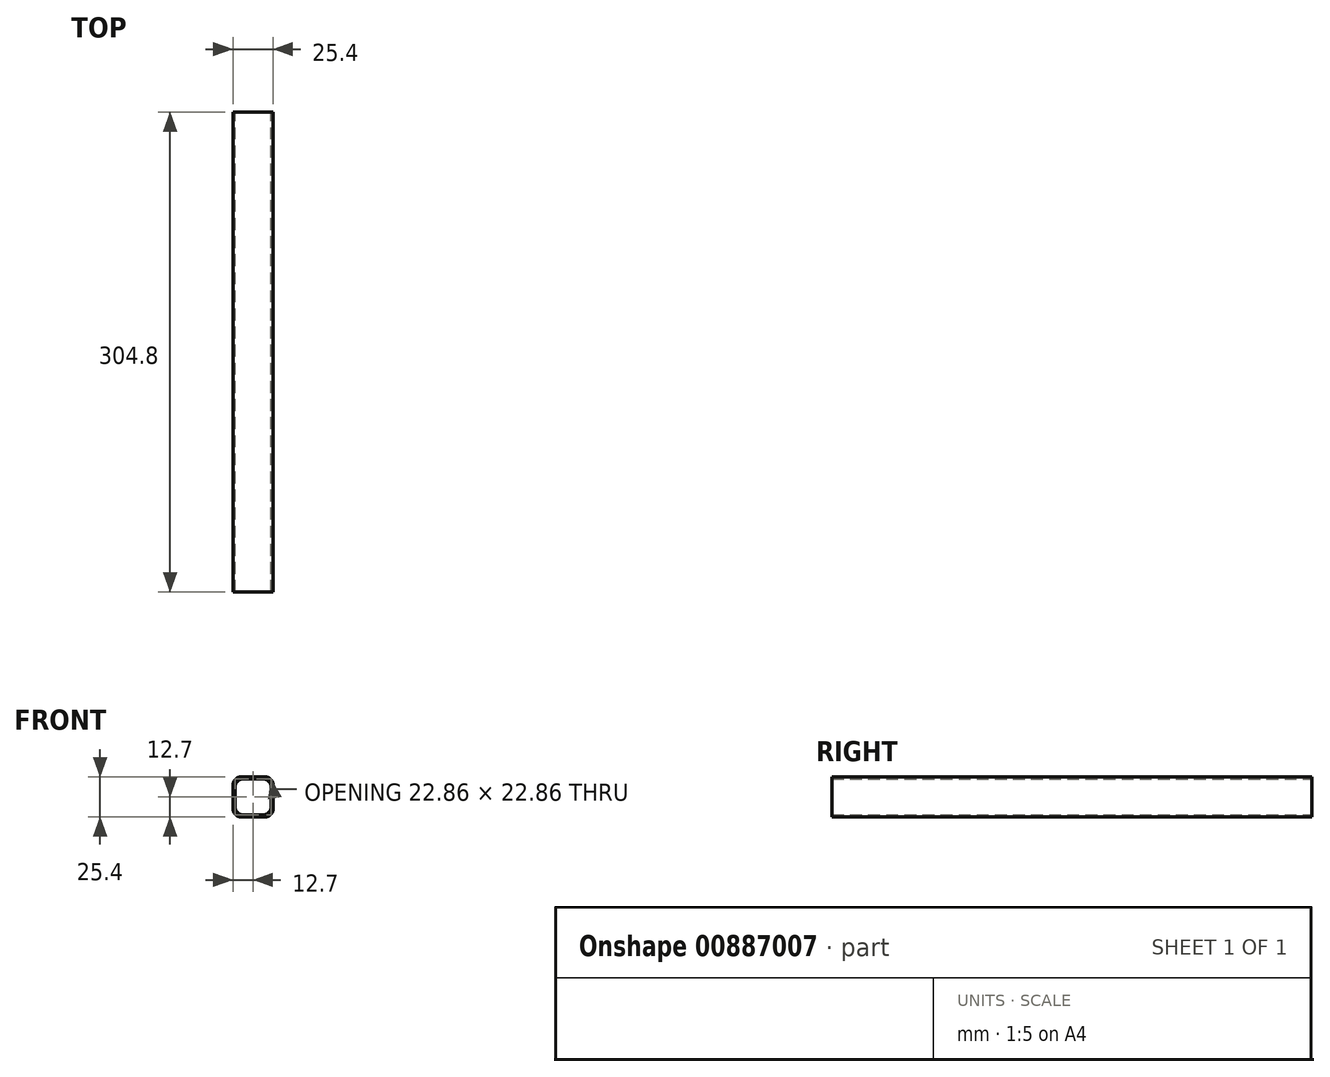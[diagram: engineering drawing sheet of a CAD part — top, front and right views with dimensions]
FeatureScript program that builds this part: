
annotation { "Feature Type Name" : "Feature", "Feature Type Description" : "" }
export const myFeature = defineFeature(function(context is Context, id is Id, definition is map)
    precondition{}
    {
        {
            var Q0;
            Q0=qCreatedBy(makeId("Front.planeOp"),FACE);
            var sketch = newSketch(context, id + "F0", { "sketchPlane" : qUnion([Q0])});
            skLineSegment(sketch, "E0.bottom", {"start": v(-12.7, 12.7) * mm, "end": v(12.7, 12.7) * mm});
            skLineSegment(sketch, "E0.top", {"start": v(-12.7, -12.7) * mm, "end": v(12.7, -12.7) * mm});
            skLineSegment(sketch, "E0.left", {"start": v(-12.7, 12.7) * mm, "end": v(-12.7, -12.7) * mm});
            skLineSegment(sketch, "E0.right", {"start": v(12.7, 12.7) * mm, "end": v(12.7, -12.7) * mm});
            skPoint(sketch, "E0.middle", {"position": v(0, 0) * mm});
            skLineSegment(sketch, "E1.bottom", {"start": v(-11.43, 11.43) * mm, "end": v(11.43, 11.43) * mm});
            skLineSegment(sketch, "E1.top", {"start": v(-11.43, -11.43) * mm, "end": v(11.43, -11.43) * mm});
            skLineSegment(sketch, "E1.left", {"start": v(-11.43, 11.43) * mm, "end": v(-11.43, -11.43) * mm});
            skLineSegment(sketch, "E1.right", {"start": v(11.43, 11.43) * mm, "end": v(11.43, -11.43) * mm});
            skSolve(sketch);
        }
        {
            var Q0;
            Q0=makeQuery(id+"F0.imprint","IMPRINT",FACE,{"disambiguationData":[TD([[makeQuery(id+"F0.imprint","IMPRINT",EDGE,{"derivedFrom":sQuery(id+"F0.wireOp",EDGE,"E0.bottom")}),-1.0]])]});
            extrude(context, id + "F1", {"entities" : qUnion([Q0]), "depth" : 304.8 * mm, "offsetDistance" : 25.4 * mm});
        }
        {
            var Q0;
            Q0=makeQuery(id+"F1.opExtrude","SWEPT_EDGE",EDGE,{"disambiguationData":[OSD([sQuery(id+"F0.wireOp",EDGE,"E1.bottom"),sQuery(id+"F0.wireOp",EDGE,"E1.left")])]});
            var Q1;
            Q1=makeQuery(id+"F1.opExtrude","SWEPT_EDGE",EDGE,{"disambiguationData":[OSD([sQuery(id+"F0.wireOp",EDGE,"E0.bottom"),sQuery(id+"F0.wireOp",EDGE,"E0.left")])]});
            var Q2;
            Q2=makeQuery(id+"F1.opExtrude","SWEPT_EDGE",EDGE,{"disambiguationData":[OSD([sQuery(id+"F0.wireOp",EDGE,"E1.bottom"),sQuery(id+"F0.wireOp",EDGE,"E1.right")])]});
            var Q3;
            Q3=makeQuery(id+"F1.opExtrude","SWEPT_EDGE",EDGE,{"disambiguationData":[OSD([sQuery(id+"F0.wireOp",EDGE,"E1.top"),sQuery(id+"F0.wireOp",EDGE,"E1.left")])]});
            var Q4;
            Q4=makeQuery(id+"F1.opExtrude","SWEPT_EDGE",EDGE,{"disambiguationData":[OSD([sQuery(id+"F0.wireOp",EDGE,"E1.top"),sQuery(id+"F0.wireOp",EDGE,"E1.right")])]});
            var Q5;
            Q5=makeQuery(id+"F1.opExtrude","SWEPT_EDGE",EDGE,{"disambiguationData":[OSD([sQuery(id+"F0.wireOp",EDGE,"E0.top"),sQuery(id+"F0.wireOp",EDGE,"E0.left")])]});
            var Q6;
            Q6=makeQuery(id+"F1.opExtrude","SWEPT_EDGE",EDGE,{"disambiguationData":[OSD([sQuery(id+"F0.wireOp",EDGE,"E0.top"),sQuery(id+"F0.wireOp",EDGE,"E0.right")])]});
            var Q7;
            Q7=makeQuery(id+"F1.opExtrude","SWEPT_EDGE",EDGE,{"disambiguationData":[OSD([sQuery(id+"F0.wireOp",EDGE,"E0.bottom"),sQuery(id+"F0.wireOp",EDGE,"E0.right")])]});
            fillet(context, id + "F2", {"entities" : qUnion([Q0, Q1, Q2, Q3, Q4, Q5, Q6, Q7]), "radius" : 5.08 * mm, "tangentPropagation" : true, "allowEdgeOverflow" : false});
        }
    });
